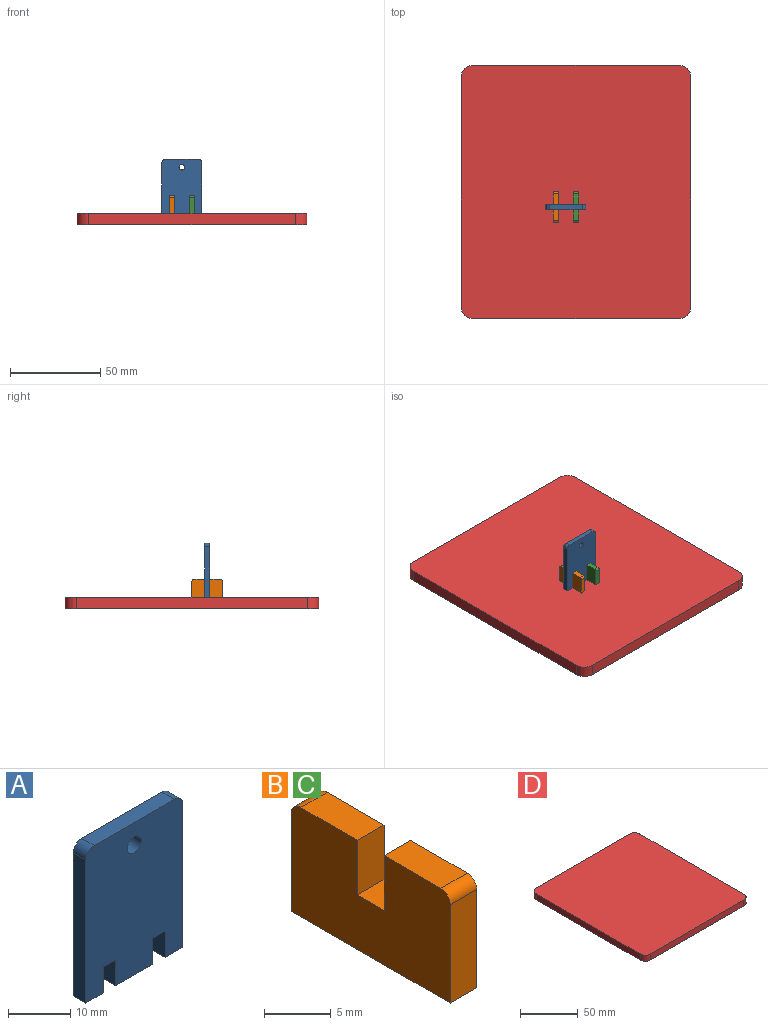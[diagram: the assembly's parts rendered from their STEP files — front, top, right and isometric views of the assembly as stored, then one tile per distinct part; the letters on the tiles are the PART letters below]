
ASSEMBLY  parts=4 mates=3
PART A: 17 faces, bbox 22x2.8x30 mm
  f0: plane 2.8x2.8mm, normal (0,0,-1), area 7.8mm2, adj f1,f13,f14,f15
  f1: plane 5.08x2.8mm, normal (-1,0,0), area 14.2mm2, adj f0,f2,f14,f15
  f2: plane 8.4x2.8mm, normal (0,0,-1), area 23.5mm2, adj f1,f3,f14,f15
  f3: plane 5.08x2.8mm, normal (1,0,0), area 14.2mm2, adj f2,f4,f14,f15
  f4: plane 2.8x2.8mm, normal (0,0,-1), area 7.8mm2, adj f3,f5,f14,f15
  f5: plane 5.08x2.8mm, normal (-1,0,0), area 14.2mm2, adj f4,f6,f14,f15
  f6: plane 4x2.8mm, normal (0,0,-1), area 11.2mm2, adj f5,f7,f14,f15
  f7: plane 28.1x2.8mm, normal (1,0,0), area 78.7mm2, adj f6,f8,f14,f15
  f8: cylinder r=1.91mm len=2.8mm, axis (0,1,0), area 8.4mm2, adj f7,f9,f14,f15
  f9: plane 18.19x2.8mm, normal (0,0,1), area 50.9mm2, adj f8,f10,f14,f15
  f10: cylinder r=1.91mm len=2.8mm, axis (0,1,0), area 8.4mm2, adj f9,f11,f14,f15
  f11: plane 28.1x2.8mm, normal (-1,0,0), area 78.7mm2, adj f10,f12,f14,f15
  f12: plane 4x2.8mm, normal (0,0,-1), area 11.2mm2, adj f11,f13,f14,f15
  f13: plane 5.08x2.8mm, normal (1,0,0), area 14.2mm2, adj f0,f12,f14,f15
  f14: plane 30x22mm, normal (0,-1,0), area 621.9mm2, adj f0,f1,f2,f3,f4,f5,f6,f7
  f15: plane 30x22mm, normal (0,1,0), area 621.9mm2, adj f0,f1,f2,f3,f4,f5,f6,f7
  f16: cylinder r=1.61mm len=3.21mm, axis (0,-1,0), area 28.2mm2, adj f14,f15
PART B: 12 faces, bbox 2.8x16.8x10 mm
  f0: plane 5x2.8mm, normal (0,1,0), area 14mm2, adj f1,f9,f10,f11
  f1: plane 6x2.8mm, normal (0,0,1), area 16.8mm2, adj f0,f2,f10,f11
  f2: cylinder r=1mm len=2.8mm, axis (-1,0,0), area 4.4mm2, adj f1,f3,f10,f11
  f3: plane 9x2.8mm, normal (0,-1,0), area 25.2mm2, adj f2,f4,f10,f11
  f4: plane 16.8x2.8mm, normal (0,0,-1), area 47mm2, adj f3,f5,f10,f11
  f5: plane 9x2.8mm, normal (0,1,0), area 25.2mm2, adj f4,f6,f10,f11
  f6: cylinder r=1mm len=2.8mm, axis (-1,0,0), area 4.4mm2, adj f5,f7,f10,f11
  f7: plane 6x2.8mm, normal (0,0,1), area 16.8mm2, adj f6,f8,f10,f11
  f8: plane 5x2.8mm, normal (0,-1,0), area 14mm2, adj f7,f9,f10,f11
  f9: plane 2.8x2.8mm, normal (0,0,1), area 7.8mm2, adj f0,f8,f10,f11
  f10: plane 16.8x10mm, normal (1,0,0), area 153.6mm2, adj f0,f1,f2,f3,f4,f5,f6,f7
  f11: plane 16.8x10mm, normal (-1,0,0), area 153.6mm2, adj f0,f1,f2,f3,f4,f5,f6,f7
PART C: same geometry as B
PART D: 10 faces, bbox 127x140x6.4 mm
  f0: cylinder r=6.35mm len=6.35mm, axis (0,0,-1), area 63.3mm2, adj f1,f7,f8,f9
  f1: plane 114.3x6.35mm, normal (0,-1,0), area 725.8mm2, adj f0,f2,f8,f9
  f2: cylinder r=6.35mm len=6.35mm, axis (0,0,-1), area 63.3mm2, adj f1,f3,f8,f9
  f3: plane 127.3x6.35mm, normal (1,0,0), area 808.4mm2, adj f2,f4,f8,f9
  f4: cylinder r=6.35mm len=6.35mm, axis (0,0,-1), area 63.3mm2, adj f3,f5,f8,f9
  f5: plane 114.3x6.35mm, normal (0,1,0), area 725.8mm2, adj f4,f6,f8,f9
  f6: cylinder r=6.35mm len=6.35mm, axis (0,0,-1), area 63.3mm2, adj f5,f7,f8,f9
  f7: plane 127.3x6.35mm, normal (-1,0,0), area 808.4mm2, adj f0,f6,f8,f9
  f8: plane 140x127mm, normal (0,0,1), area 17745.4mm2, adj f0,f1,f2,f3,f4,f5,f6,f7
  f9: plane 140x127mm, normal (0,0,-1), area 17745.4mm2, adj f0,f1,f2,f3,f4,f5,f6,f7
PLACE A t=(-123.3,18.56,-45.52)mm
PLACE B t=(-122.18,1.58,-16.06)mm
PLACE C t=(-110.98,1.58,-16.06)mm
PLACE D t=(-3.76,46.99,29.59)mm
MATE fastened C.f4 <-> D.f8  axis (0,0,-1) through (-0.48,88.56,35.94)mm
MATE fastened A.f4 <-> C.f9  axis (0,0,-1) through (-0.48,80.16,40.94)mm
MATE fastened A.f0 <-> B.f9  axis (0,0,-1) through (-11.68,80.16,40.94)mm
